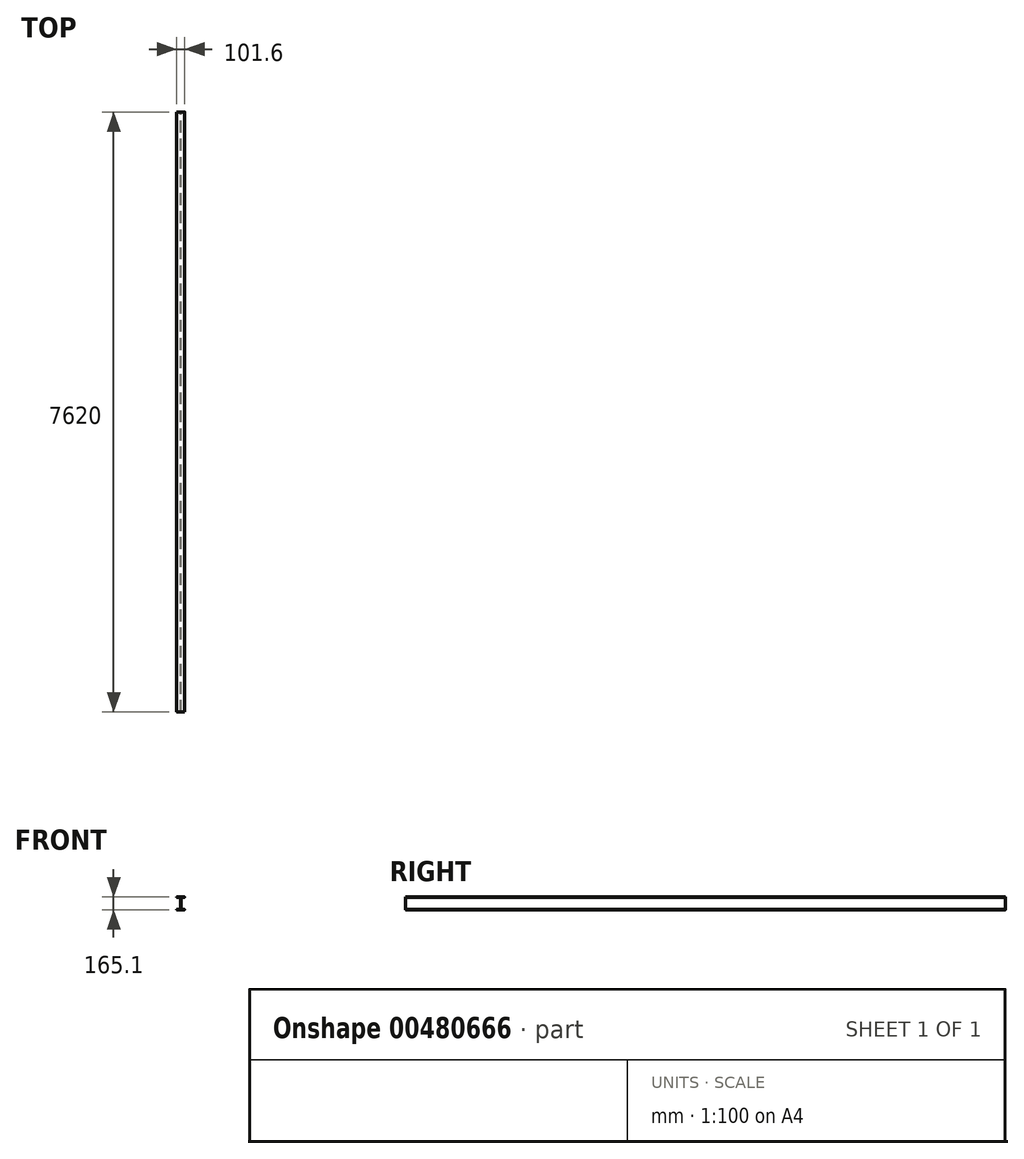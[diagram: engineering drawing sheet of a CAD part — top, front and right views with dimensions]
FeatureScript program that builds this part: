
annotation { "Feature Type Name" : "Feature", "Feature Type Description" : "" }
export const myFeature = defineFeature(function(context is Context, id is Id, definition is map)
    precondition{}
    {
        {
            var Q0;
            Q0=qCreatedBy(makeId("Front.planeOp"),FACE);
            var sketch = newSketch(context, id + "F0", { "sketchPlane" : qUnion([Q0])});
            skLineSegment(sketch, "E0", {"start": v(0, 137.16) * mm, "end": v(0, -15.24) * mm, "construction": true});
            skLineSegment(sketch, "E1", {"start": v(-50.55, 137.16) * mm, "end": v(-9.53, 137.16) * mm});
            skLineSegment(sketch, "E2", {"start": v(-50.55, -15.24) * mm, "end": v(-9.52, -15.24) * mm});
            skLineSegment(sketch, "E3.0", {"start": v(-50.55, -21.59) * mm, "end": v(50.55, -21.59) * mm});
            skLineSegment(sketch, "E4.0", {"start": v(-50.55, 143.5) * mm, "end": v(50.55, 143.5) * mm});
            skLineSegment(sketch, "E5.0", {"start": v(-3.17, 130.8) * mm, "end": v(-3.17, -8.89) * mm});
            skLineSegment(sketch, "E6.0", {"start": v(3.18, 130.8) * mm, "end": v(3.18, -8.89) * mm});
            skLineSegment(sketch, "E7", {"start": v(-50.8, -21.34) * mm, "end": v(-50.8, -15.5) * mm});
            skLineSegment(sketch, "E8", {"start": v(50.8, -15.5) * mm, "end": v(50.8, -21.34) * mm});
            skLineSegment(sketch, "E9", {"start": v(50.8, 137.41) * mm, "end": v(50.8, 143.26) * mm});
            skLineSegment(sketch, "E10", {"start": v(-50.8, 143.26) * mm, "end": v(-50.8, 137.41) * mm});
            skLineSegment(sketch, "E11.trimOffspring", {"start": v(9.53, 137.16) * mm, "end": v(50.55, 137.16) * mm});
            skLineSegment(sketch, "E12.trimOffspring", {"start": v(9.53, -15.24) * mm, "end": v(50.55, -15.24) * mm});
            skPoint(sketch, "E13.visualSharp", {"position": v(-3.18, 137.16) * mm});
            skArc(sketch, "E13.filletArc", {"start": v(-3.17, 130.8) * mm, "mid": v(-5.03, 135.3) * mm, "end": v(-9.53, 137.16) * mm});
            skPoint(sketch, "E14.visualSharp", {"position": v(3.18, 137.16) * mm});
            skArc(sketch, "E14.filletArc", {"start": v(9.53, 137.16) * mm, "mid": v(5.03, 135.3) * mm, "end": v(3.18, 130.8) * mm});
            skPoint(sketch, "E15.visualSharp", {"position": v(-3.17, -15.24) * mm});
            skArc(sketch, "E15.filletArc", {"start": v(-9.52, -15.24) * mm, "mid": v(-5.03, -13.38) * mm, "end": v(-3.17, -8.89) * mm});
            skPoint(sketch, "E16.visualSharp", {"position": v(3.18, -15.24) * mm});
            skArc(sketch, "E16.filletArc", {"start": v(3.18, -8.89) * mm, "mid": v(5.03, -13.38) * mm, "end": v(9.53, -15.24) * mm});
            skPoint(sketch, "E17.visualSharp", {"position": v(-50.8, -15.24) * mm});
            skArc(sketch, "E17.filletArc", {"start": v(-50.55, -15.24) * mm, "mid": v(-50.73, -15.31) * mm, "end": v(-50.8, -15.5) * mm});
            skPoint(sketch, "E18.visualSharp", {"position": v(-50.8, -21.59) * mm});
            skArc(sketch, "E18.filletArc", {"start": v(-50.8, -21.34) * mm, "mid": v(-50.73, -21.52) * mm, "end": v(-50.55, -21.59) * mm});
            skPoint(sketch, "E19.visualSharp", {"position": v(50.8, -21.59) * mm});
            skArc(sketch, "E19.filletArc", {"start": v(50.55, -21.59) * mm, "mid": v(50.73, -21.52) * mm, "end": v(50.8, -21.34) * mm});
            skPoint(sketch, "E20.visualSharp", {"position": v(50.8, -15.24) * mm});
            skArc(sketch, "E20.filletArc", {"start": v(50.8, -15.5) * mm, "mid": v(50.73, -15.31) * mm, "end": v(50.55, -15.24) * mm});
            skPoint(sketch, "E21.visualSharp", {"position": v(50.8, 137.16) * mm});
            skArc(sketch, "E21.filletArc", {"start": v(50.55, 137.16) * mm, "mid": v(50.73, 137.23) * mm, "end": v(50.8, 137.41) * mm});
            skPoint(sketch, "E22.visualSharp", {"position": v(50.8, 143.5) * mm});
            skArc(sketch, "E22.filletArc", {"start": v(50.8, 143.26) * mm, "mid": v(50.73, 143.44) * mm, "end": v(50.55, 143.5) * mm});
            skPoint(sketch, "E23.visualSharp", {"position": v(-50.8, 143.5) * mm});
            skArc(sketch, "E23.filletArc", {"start": v(-50.55, 143.5) * mm, "mid": v(-50.73, 143.44) * mm, "end": v(-50.8, 143.26) * mm});
            skPoint(sketch, "E24.visualSharp", {"position": v(-50.8, 137.16) * mm});
            skArc(sketch, "E24.filletArc", {"start": v(-50.8, 137.41) * mm, "mid": v(-50.73, 137.23) * mm, "end": v(-50.55, 137.16) * mm});
            skSolve(sketch);
        }
        {
            var Q0;
            Q0=makeQuery(id+"F0.imprint","IMPRINT",FACE,{"disambiguationData":[TD([[makeQuery(id+"F0.imprint","IMPRINT",EDGE,{"derivedFrom":sQuery(id+"F0.wireOp",EDGE,"E1")}),1.0]])]});
            extrude(context, id + "F1", {"entities" : qUnion([Q0]), "depth" : 7620 * mm});
        }
    });
